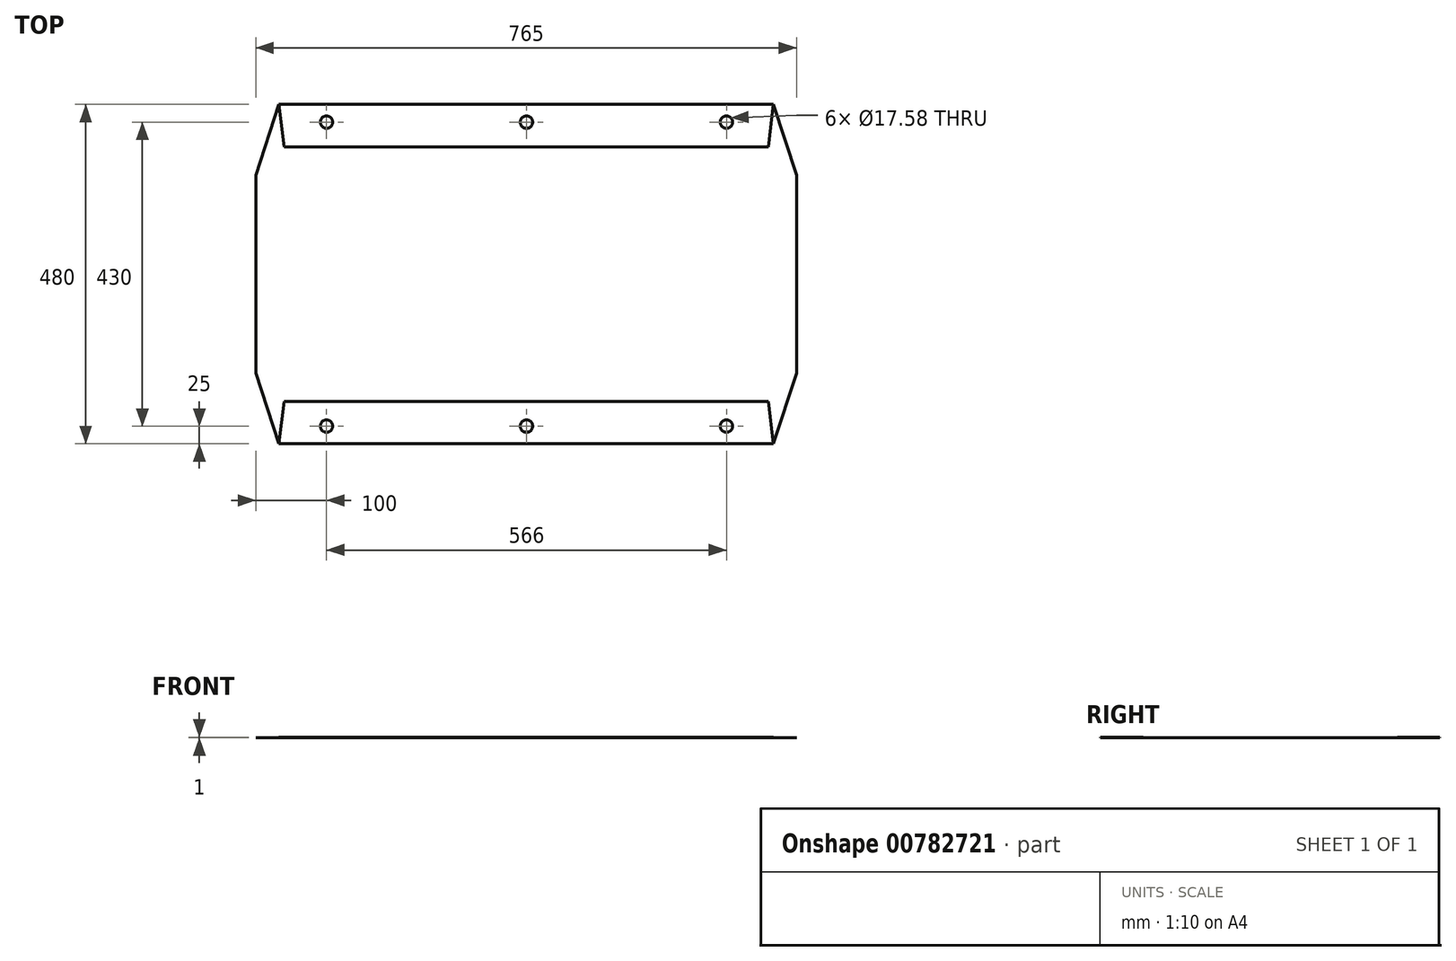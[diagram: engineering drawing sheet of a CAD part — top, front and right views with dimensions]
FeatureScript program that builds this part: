
annotation { "Feature Type Name" : "Feature", "Feature Type Description" : "" }
export const myFeature = defineFeature(function(context is Context, id is Id, definition is map)
    precondition{}
    {
        {
            var Q0;
            Q0=qCreatedBy(makeId("Top.planeOp"),FACE);
            var sketch = newSketch(context, id + "F0", { "sketchPlane" : qUnion([Q0])});
            skLineSegment(sketch, "E0", {"start": v(-700, 0) * mm, "end": v(0, 0) * mm});
            skLineSegment(sketch, "E1", {"start": v(0, 0) * mm, "end": v(32.5, -100) * mm});
            skLineSegment(sketch, "E2", {"start": v(32.5, -100) * mm, "end": v(32.5, -240) * mm});
            skLineSegment(sketch, "E3", {"start": v(-732.5, -240) * mm, "end": v(-732.5, -100) * mm});
            skLineSegment(sketch, "E4", {"start": v(-732.5, -100) * mm, "end": v(-700, 0) * mm});
            skLineSegment(sketch, "E5", {"start": v(-732.5, -240) * mm, "end": v(32.5, -240) * mm, "construction": true});
            skLineSegment(sketch, "E6.MirrorCS", {"start": v(-732.5, -240) * mm, "end": v(-732.5, -380) * mm});
            skLineSegment(sketch, "E7.MirrorCS", {"start": v(-732.5, -380) * mm, "end": v(-700, -480) * mm});
            skLineSegment(sketch, "E8.MirrorCS", {"start": v(-700, -480) * mm, "end": v(0, -480) * mm});
            skLineSegment(sketch, "E9.MirrorCS", {"start": v(0, -480) * mm, "end": v(32.5, -380) * mm});
            skLineSegment(sketch, "E10.MirrorCS", {"start": v(32.5, -380) * mm, "end": v(32.5, -240) * mm});
            skSolve(sketch);
        }
        {
            var Q0;
            Q0=qSketchRegion(id+"F0",true);
            extrude(context, id + "F1", {"entities" : qUnion([Q0]), "depth" : .5 * mm, "offsetDistance" : 25 * mm});
        }
        {
            var Q0;
            Q0=makeQuery(id+"F1.opExtrude","CAP_FACE",FACE,{"disambiguationData":[OSD([sQuery(id+"F0.wireOp",EDGE,"E0"),sQuery(id+"F0.wireOp",EDGE,"E1"),sQuery(id+"F0.wireOp",EDGE,"E2"),sQuery(id+"F0.wireOp",EDGE,"4DUcCnAT-J5pK-TljG-z9Yb-rQMT2OcHOQ3j"),sQuery(id+"F0.wireOp",EDGE,"E3"),sQuery(id+"F0.wireOp",EDGE,"E4")])],"isStart":false});
            var sketch = newSketch(context, id + "F2", { "sketchPlane" : qUnion([Q0])});
            skLineSegment(sketch, "E11", {"start": v(-700, 0) * mm, "end": v(-692.5, -60) * mm});
            skLineSegment(sketch, "E12", {"start": v(-692.5, -60) * mm, "end": v(-7.5, -60) * mm});
            skLineSegment(sketch, "E13", {"start": v(-7.5, -60) * mm, "end": v(0, 0) * mm});
            skLineSegment(sketch, "E14", {"start": v(0, 0) * mm, "end": v(-700, 0) * mm});
            skLineSegment(sketch, "E15", {"start": v(-732.5, -240) * mm, "end": v(32.5, -240) * mm, "construction": true});
            skLineSegment(sketch, "E16.MirrorCS", {"start": v(-700, -480) * mm, "end": v(-692.5, -420) * mm});
            skLineSegment(sketch, "E17.MirrorCS", {"start": v(-692.5, -420) * mm, "end": v(-7.5, -420) * mm});
            skLineSegment(sketch, "E18.MirrorCS", {"start": v(-7.5, -420) * mm, "end": v(0, -480) * mm});
            skLineSegment(sketch, "E19.MirrorCS", {"start": v(0, -480) * mm, "end": v(-700, -480) * mm});
            skSolve(sketch);
        }
        {
            var Q0;
            Q0=qSketchRegion(id+"F2",true);
            extrude(context, id + "F3", {"entities" : qUnion([Q0]), "operationType" : NewBodyOperationType.ADD, "depth" : .5 * mm, "offsetDistance" : 25 * mm});
        }
        {
            var Q0;
            Q0=makeQuery(id+"F3.opExtrude","CAP_FACE",FACE,{"disambiguationData":[OSD([sQuery(id+"F2.wireOp",EDGE,"E11"),sQuery(id+"F2.wireOp",EDGE,"E12"),sQuery(id+"F2.wireOp",EDGE,"E13"),sQuery(id+"F2.wireOp",EDGE,"E14")])],"isStart":false});
            var sketch = newSketch(context, id + "F4", { "sketchPlane" : qUnion([Q0])});
            skCircle(sketch, "E20", {"center": v(-632.5, -25) * mm, "radius": 8.79 * mm});
            skCircle(sketch, "E21.0.1.0", {"center": v(-632.5, -455) * mm, "radius": 8.79 * mm});
            skCircle(sketch, "E21.1.0.0", {"center": v(-349.5, -25) * mm, "radius": 8.79 * mm});
            skCircle(sketch, "E21.1.1.0", {"center": v(-349.5, -455) * mm, "radius": 8.79 * mm});
            skLineSegment(sketch, "E21.direction1", {"start": v(-632.5, -25) * mm, "end": v(-349.5, -25) * mm, "construction": true});
            skLineSegment(sketch, "E21.direction2", {"start": v(-632.5, -25) * mm, "end": v(-632.5, -455) * mm, "construction": true});
            skCircle(sketch, "E22.0.2.0", {"center": v(-66.5, -25) * mm, "radius": 8.79 * mm});
            skCircle(sketch, "E22.0.2.1", {"center": v(-66.5, -455) * mm, "radius": 8.79 * mm});
            skSolve(sketch);
        }
        {
            var Q0;
            Q0 = qSketchRegion(id + "F4", true);
            extrude(context, id + "F5", {"entities" : qUnion([Q0]), "operationType" : NewBodyOperationType.REMOVE, "endBound" : BoundingType.THROUGH_ALL, "oppositeDirection" : true, "depth" : 25 * mm, "offsetDistance" : 25 * mm});
        }
    });
